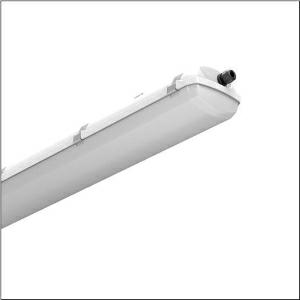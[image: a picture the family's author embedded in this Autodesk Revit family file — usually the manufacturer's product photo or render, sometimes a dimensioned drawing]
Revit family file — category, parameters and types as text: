
# Revit family: monsun_ex_51fxb1dp470a
name_source: partatom
category: Lighting Fixtures
units: mm (PartAtom-declared; Revit-internal decimal feet)

## family parameters
Cut with Voids When Loaded = No
Host = Face
Light Source = No
Part Type = Normal
Room Calculation Point = No
Round Connector Dimension = Use Diameter
Shared = No

## types (1)
- Monsun Ex (1 x LED, 7310 lm, 43.8 W, 4000K)
    Apparent Load = 44 VA
    CIE Flux Codes = 61 86 97 100 100
    Color Rendering = 80
    Color Temperature = 4000K
    Default Elevation = 1800 mm
    Description = Monsun Ex, damp-proof luminaire, primary optical cover: cover, of PC, UV-stabilised, opal, light emission: direct distribution, primary light characteristic: symmetric, installation type: surface-mounted, LED, rated luminous flux: 7.310lm, luminous efficacy: 167lm/W, light colour: 840, colour temperature: 4000K, control gear: DALI 2, with terminal, 5-pole, max. 2.5mm², through-wiring: 7x 2.5mm², mains connection: 220..240V, AC, 50/60Hz, rated input power: 44W, housing, of PC, light grey (RAL 7035), incl. blanking plug, incl. 2x Ex cable gland M20 for cable diameter 7..12mm with sealing, length: 1.580mm, width: 155mm, height: 105mm, clip for enclosure, of stainless steel, protection rating (complete): IP66, insulation class (complete): insulation class I (protective earthing), certification: CE, explosion class: zone2,22 II 3G Ex nR IIC T6 GC, II 3D Ex tc IIIC T80°C Dc, impact resistance: IK10, permissible operating ambient temperature: -20..+60°C, LABS conformity tested according to VDMA 24364:2018-05, contact your sales advisor before using the luminaires in applications with unclear chemical exposure, large temperature fluctuations or condensation-forming humidity, packaging unit: 1 piece
    Height = 105 mm
    Lamp = 1 x LED
    Lamp Light Flux = 7310 lm
    Lamp Power = 43.8 W
    Lamp count = 1
    Length = 1580 mm
    Luminous efficacy = 167 lm/W
    Manufacturer = Siteco
    ModVariant = No
    Model = 51FXB1DP470A
    Mounting Place = Ceiling
    Mounting Type = Surface mounted
    Number of Poles = 1
    OnlyDefault = Yes
    Power Factor = 1
    Product Name = Monsun Ex
    Product group = damp-proof luminaire
    ProductGroupID = 300
    Protection Class = Protection class I
    Protection Degree = IP 66
    RLX_Detail_Level = 1
    RLX_Emergency_Light_Flux = 0 lm
    RLX_Emergency_Type = 0
    RLX_Emergency_Type_DB = No
    RlxData = <blob elided: 41749 chars, md5=69daf247>
    Socket = socket
    Standby Power = 0 W
    System Light Flux = 7310 lm
    System Power = 44 W
    Type Comments = Product without accessories
    Type Image = l_1258882.jpg
    URL = http://relux.com
    VarID = ---
    Voltage = 0 V
    Weight = 0.00 kg
    Width = 155 mm

## geometry (parser evidence)
native form markers: Blend x4, Sweep x9
no freeform markers — native parametric forms only
